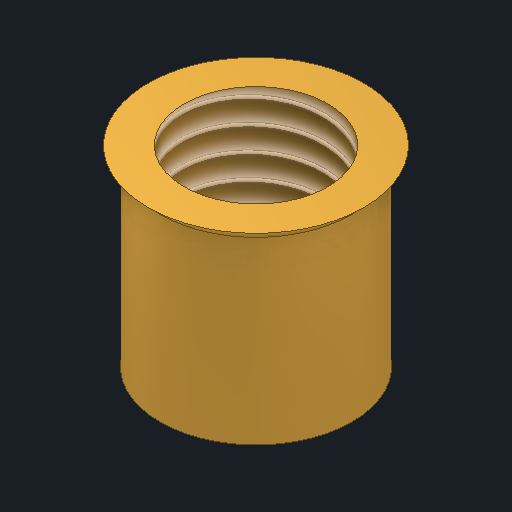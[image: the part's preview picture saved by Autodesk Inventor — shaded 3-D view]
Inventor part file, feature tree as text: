
AUTODESK INVENTOR PART (.ipt)
format: ipt  version: 2025 (Build 290162010, 162A)  size: 160,768 bytes
history: native  units: mm
features: extrude x2, sketch x2, chamfer x1, thread x1
ambient origin geometry x8: Origin, YZ Plane, XZ Plane, XY Plane, X Axis, Y Axis, Z Axis, Center Point
bodies: Solid1 (feature_tree)
feature tree (6):
  extrude  "Extrusion1"  Depth=4.0mm
  extrude  "Extrusion2"  Depth=4.0mm
  chamfer  "Chamfer1"  Distance=0.25mm
  thread  "Thread1"  [1 undecoded]
  sketch  "Sketch1"  dims[d0=4.0mm d1=3.0mm]
  sketch  "Sketch2"  dims[d2=4.0mm d3=0.0mm d4=4.5mm d5=0.25mm d6=0.0mm d7=0.25mm d8=2.0mm d9=45.0deg d10=4.0mm d11=0.0mm]
note: 1 required parameter value undecoded (feature->parameter linkage not recoverable at this tier; creation-order binding heuristic only, values carry confidence <= 0.55)
